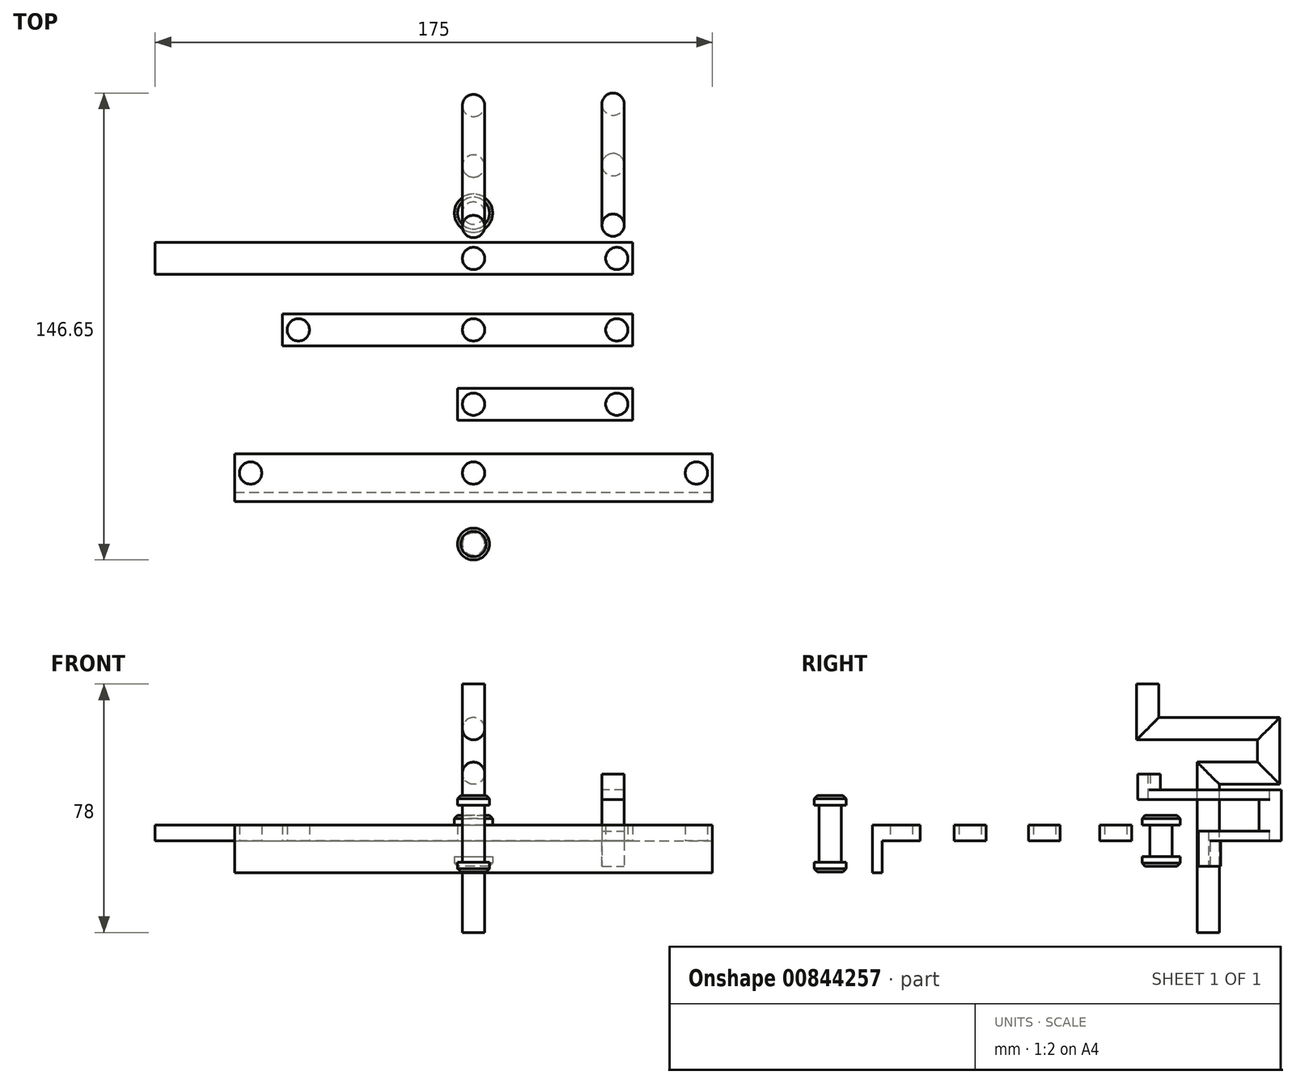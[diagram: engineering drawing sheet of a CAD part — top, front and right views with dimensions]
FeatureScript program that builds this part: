
annotation { "Feature Type Name" : "Feature", "Feature Type Description" : "" }
export const myFeature = defineFeature(function(context is Context, id is Id, definition is map)
    precondition{}
    {
        {
            var Q0;
            Q0=qCreatedBy(makeId("Top.planeOp"),FACE);
            var sketch = newSketch(context, id + "F0", { "sketchPlane" : qUnion([Q0])});
            skLineSegment(sketch, "E0.bottom", {"start": v(50, -5) * mm, "end": v(-60, -5) * mm});
            skLineSegment(sketch, "E0.top", {"start": v(50, 5) * mm, "end": v(-60, 5) * mm});
            skLineSegment(sketch, "E0.left", {"start": v(50, -5) * mm, "end": v(50, 5) * mm});
            skLineSegment(sketch, "E0.right", {"start": v(-60, -5) * mm, "end": v(-60, 5) * mm});
            skPoint(sketch, "E0.middle", {"position": v(0, 0) * mm});
            skCircle(sketch, "E1", {"center": v(-55, 0) * mm, "radius": 3.5 * mm});
            skCircle(sketch, "E2", {"center": v(45, 0) * mm, "radius": 3.5 * mm});
            skPoint(sketch, "E2.centerSnap0", {"position": v(50, 0) * mm});
            skCircle(sketch, "E3", {"center": v(0, 0) * mm, "radius": 3.5 * mm});
            skSolve(sketch);
        }
        {
            var Q0;
            Q0=makeQuery(id+"F0.imprint","IMPRINT",FACE,{"disambiguationData":[TD([[makeQuery(id+"F0.imprint","IMPRINT",EDGE,{"derivedFrom":sQuery(id+"F0.wireOp",EDGE,"E0.bottom")}),-1.0]])]});
            extrude(context, id + "F1", {"entities" : qUnion([Q0]), "depth" : 5 * mm, "offsetDistance" : 25 * mm});
        }
        {
            var Q0;
            Q0=qCreatedBy(makeId("Top.planeOp"),FACE);
            var sketch = newSketch(context, id + "F2", { "sketchPlane" : qUnion([Q0])});
            skLineSegment(sketch, "E4.bottom", {"start": v(-100, 27.42) * mm, "end": v(50, 27.42) * mm});
            skLineSegment(sketch, "E4.top", {"start": v(-100, 17.42) * mm, "end": v(50, 17.42) * mm});
            skLineSegment(sketch, "E4.left", {"start": v(-100, 27.42) * mm, "end": v(-100, 17.42) * mm});
            skLineSegment(sketch, "E4.right", {"start": v(50, 27.42) * mm, "end": v(50, 17.42) * mm});
            skLineSegment(sketch, "E5", {"start": v(-100, 22.42) * mm, "end": v(50, 22.42) * mm, "construction": true});
            skCircle(sketch, "E6", {"center": v(0, 22.42) * mm, "radius": 3.5 * mm});
            skCircle(sketch, "E7", {"center": v(45, 22.42) * mm, "radius": 3.5 * mm});
            skSolve(sketch);
        }
        {
            var Q0;
            Q0=makeQuery(id+"F2.imprint","IMPRINT",FACE,{"disambiguationData":[TD([[makeQuery(id+"F2.imprint","IMPRINT",EDGE,{"derivedFrom":sQuery(id+"F2.wireOp",EDGE,"E4.bottom")}),-1.0]])]});
            extrude(context, id + "F3", {"entities" : qUnion([Q0]), "depth" : 5 * mm, "offsetDistance" : 25 * mm});
        }
        {
            var Q0;
            Q0=qCreatedBy(makeId("Top.planeOp"),FACE);
            var sketch = newSketch(context, id + "F4", { "sketchPlane" : qUnion([Q0])});
            skLineSegment(sketch, "E8.bottom", {"start": v(-5, -18.35) * mm, "end": v(50, -18.35) * mm});
            skLineSegment(sketch, "E8.top", {"start": v(-5, -28.35) * mm, "end": v(50, -28.35) * mm});
            skLineSegment(sketch, "E8.left", {"start": v(-5, -18.35) * mm, "end": v(-5, -28.35) * mm});
            skLineSegment(sketch, "E8.right", {"start": v(50, -18.35) * mm, "end": v(50, -28.35) * mm});
            skLineSegment(sketch, "E9", {"start": v(-5, -23.35) * mm, "end": v(50, -23.35) * mm, "construction": true});
            skCircle(sketch, "E10", {"center": v(0, -23.35) * mm, "radius": 3.5 * mm});
            skCircle(sketch, "E11", {"center": v(45, -23.35) * mm, "radius": 3.5 * mm});
            skSolve(sketch);
        }
        {
            var Q0;
            Q0=makeQuery(id+"F4.imprint","IMPRINT",FACE,{"disambiguationData":[TD([[makeQuery(id+"F4.imprint","IMPRINT",EDGE,{"derivedFrom":sQuery(id+"F4.wireOp",EDGE,"E8.bottom")}),-1.0]])]});
            extrude(context, id + "F5", {"entities" : qUnion([Q0]), "depth" : 5 * mm, "offsetDistance" : 25 * mm});
        }
        {
            var Q0;
            Q0=qCreatedBy(makeId("Top.planeOp"),FACE);
            var sketch = newSketch(context, id + "F6", { "sketchPlane" : qUnion([Q0])});
            skLineSegment(sketch, "E12.bottom", {"start": v(-75, -38.96) * mm, "end": v(75, -38.96) * mm});
            skLineSegment(sketch, "E12.top", {"start": v(-75, -53.96) * mm, "end": v(75, -53.96) * mm});
            skLineSegment(sketch, "E12.left", {"start": v(-75, -38.96) * mm, "end": v(-75, -53.96) * mm});
            skLineSegment(sketch, "E12.right", {"start": v(75, -38.96) * mm, "end": v(75, -53.96) * mm});
            skLineSegment(sketch, "E13", {"start": v(-75, -50.96) * mm, "end": v(75, -50.96) * mm});
            skLineSegment(sketch, "E14", {"start": v(-75, -44.96) * mm, "end": v(75, -44.96) * mm, "construction": true});
            skCircle(sketch, "E15", {"center": v(-70, -44.96) * mm, "radius": 3.5 * mm});
            skCircle(sketch, "E16", {"center": v(0, -44.96) * mm, "radius": 3.5 * mm});
            skCircle(sketch, "E17", {"center": v(70, -44.96) * mm, "radius": 3.5 * mm});
            skSolve(sketch);
        }
        {
            var Q0;
            {var subQ1=sQuery(id+"F6.wireOp",EDGE,"E12.top");Q0=makeQuery(id+"F6.imprint","IMPRINT",FACE,{"disambiguationData":[TD([[makeQuery(id+"F6.imprint","IMPRINT",EDGE,{"derivedFrom":subQ1}),1.0]])]});}
            var Q1;
            {var subQ0=sQuery(id+"F6.wireOp",EDGE,"E16");var subQ1=sQuery(id+"F6.wireOp",EDGE,"E13");var subQ2=makeQuery(id+"F6.imprint","INTERSECT",VERTEX,{"disambiguationData":[OD(0.0)],"derivedFrom":[subQ1,subQ0]});Q1=makeQuery(id+"F6.imprint","IMPRINT",FACE,{"disambiguationData":[TD([[makeQuery(id+"F6.imprint","IMPRINT",EDGE,{"disambiguationData":[TD([[subQ2,-1.0]])],"derivedFrom":subQ1}),-1.0]])]});}
            var Q2;
            {var subQ0=sQuery(id+"F6.wireOp",EDGE,"E15");var subQ1=sQuery(id+"F6.wireOp",EDGE,"E13");var subQ2=makeQuery(id+"F6.imprint","INTERSECT",VERTEX,{"disambiguationData":[OD(0.0)],"derivedFrom":[subQ1,subQ0]});Q2=makeQuery(id+"F6.imprint","IMPRINT",FACE,{"disambiguationData":[TD([[makeQuery(id+"F6.imprint","IMPRINT",EDGE,{"disambiguationData":[TD([[subQ2,-1.0]])],"derivedFrom":subQ1}),-1.0]])]});}
            var Q3;
            {var subQ0=sQuery(id+"F6.wireOp",EDGE,"E17");var subQ1=sQuery(id+"F6.wireOp",EDGE,"E13");var subQ2=makeQuery(id+"F6.imprint","INTERSECT",VERTEX,{"disambiguationData":[OD(0.0)],"derivedFrom":[subQ1,subQ0]});Q3=makeQuery(id+"F6.imprint","IMPRINT",FACE,{"disambiguationData":[TD([[makeQuery(id+"F6.imprint","IMPRINT",EDGE,{"disambiguationData":[TD([[subQ2,-1.0]])],"derivedFrom":subQ1}),-1.0]])]});}
            extrude(context, id + "F7", {"entities" : qUnion([Q0, Q1, Q2, Q3]), "oppositeDirection" : true, "depth" : 10 * mm, "offsetDistance" : 25 * mm});
        }
        {
            var Q0;
            {var subQ6=sQuery(id+"F6.wireOp",EDGE,"E12.bottom");Q0=makeQuery(id+"F6.imprint","IMPRINT",FACE,{"disambiguationData":[TD([[makeQuery(id+"F6.imprint","IMPRINT",EDGE,{"derivedFrom":subQ6}),-1.0]])]});}
            var Q1;
            {var subQ1=sQuery(id+"F6.wireOp",EDGE,"E12.top");Q1=makeQuery(id+"F6.imprint","IMPRINT",FACE,{"disambiguationData":[TD([[makeQuery(id+"F6.imprint","IMPRINT",EDGE,{"derivedFrom":subQ1}),1.0]])]});}
            extrude(context, id + "F8", {"entities" : qUnion([Q0, Q1]), "operationType" : NewBodyOperationType.ADD, "depth" : 5 * mm, "offsetDistance" : 25 * mm});
        }
        {
            var Q0;
            Q0=qCreatedBy(makeId("Right.planeOp"),FACE);
            var sketch = newSketch(context, id + "F9", { "sketchPlane" : qUnion([Q0])});
            skLineSegment(sketch, "E18", {"start": v(36.67, -15.56) * mm, "end": v(36.67, 16.44) * mm, "construction": true});
            skLineSegment(sketch, "E19.MirrorCS", {"start": v(30.67, -5) * mm, "end": v(30.67, -8) * mm});
            skLineSegment(sketch, "E20.MirrorCS", {"start": v(33.17, -5) * mm, "end": v(30.67, -5) * mm});
            skLineSegment(sketch, "E21.MirrorCS", {"start": v(30.67, -8) * mm, "end": v(36.67, -8) * mm});
            skLineSegment(sketch, "E22.MirrorCS", {"start": v(33.17, 0) * mm, "end": v(33.17, -5) * mm});
            skLineSegment(sketch, "E23.MirrorCS", {"start": v(30.67, 8) * mm, "end": v(36.67, 8) * mm});
            skLineSegment(sketch, "E24.MirrorCS", {"start": v(30.67, 5) * mm, "end": v(30.67, 8) * mm});
            skLineSegment(sketch, "E25.MirrorCS", {"start": v(33.17, 0) * mm, "end": v(33.17, 5) * mm});
            skLineSegment(sketch, "E26.MirrorCS", {"start": v(33.17, 5) * mm, "end": v(30.67, 5) * mm});
            skLineSegment(sketch, "E27", {"start": v(36.67, 8) * mm, "end": v(36.67, -8) * mm});
            skSolve(sketch);
        }
        {
            var Q0;
            Q0=makeQuery(id+"F9.imprint","IMPRINT",FACE,{"disambiguationData":[TD([[makeQuery(id+"F9.imprint","IMPRINT",EDGE,{"derivedFrom":sQuery(id+"F9.wireOp",EDGE,"E19.MirrorCS")}),1.0]])]});
            var Q1;
            Q1=sQuery(id+"F9.wireOp",EDGE,"E18");
            revolve(context, id + "F10", {"surfaceOperationType" : NewSurfaceOperationType.NEW, "entities" : qUnion([Q0]), "axis" : qUnion([Q1]), "revolveType" : RevolveType.FULL});
        }
        {
            var Q0;
            Q0=makeQuery(id+"F10.opRevolve","SWEPT_EDGE",EDGE,{"disambiguationData":[OSD([sQuery(id+"F9.wireOp",EDGE,"E23.MirrorCS"),sQuery(id+"F9.wireOp",EDGE,"E24.MirrorCS")])]});
            var Q1;
            Q1=makeQuery(id+"F10.opRevolve","SWEPT_EDGE",EDGE,{"disambiguationData":[OSD([sQuery(id+"F9.wireOp",EDGE,"E19.MirrorCS"),sQuery(id+"F9.wireOp",EDGE,"E21.MirrorCS")])]});
            chamfer(context, id + "F11", {"entities" : qUnion([Q0, Q1]), "width" : 1 * mm, "tangentPropagation" : true});
        }
        {
            var Q0;
            Q0=qCreatedBy(makeId("Right.planeOp"),FACE);
            var sketch = newSketch(context, id + "F12", { "sketchPlane" : qUnion([Q0])});
            skLineSegment(sketch, "E28", {"start": v(51.47, 21.22) * mm, "end": v(51.47, -28.78) * mm});
            skLineSegment(sketch, "E29", {"start": v(51.47, 21.22) * mm, "end": v(70.47, 21.22) * mm});
            skLineSegment(sketch, "E30", {"start": v(70.47, 21.22) * mm, "end": v(70.47, 35.22) * mm});
            skLineSegment(sketch, "E31", {"start": v(70.47, 35.22) * mm, "end": v(32.47, 35.22) * mm});
            skLineSegment(sketch, "E32", {"start": v(32.47, 35.22) * mm, "end": v(32.47, 49.22) * mm});
            skSolve(sketch);
        }
        {
            var Q0;
            Q0=qCreatedBy(makeId("Top.planeOp"),FACE);
            var Q1;
            Q1=sQuery(id+"F12.wireOp",VERTEX,"E28.end");
            cPlane(context, id + "F13", {"entities" : qUnion([Q0, Q1]), "cplaneType" : CPlaneType.PLANE_POINT, "offset" : 25 * mm, "width" : 150 * mm, "height" : 150 * mm});
        }
        {
            var Q0;
            Q0=qCreatedBy(id+"F13.planeOp",FACE);
            var sketch = newSketch(context, id + "F14", { "sketchPlane" : qUnion([Q0])});
            skCircle(sketch, "E33", {"center": v(0, 51.47) * mm, "radius": 3.5 * mm});
            skSolve(sketch);
        }
        {
            var Q0;
            Q0=makeQuery(id+"F14.imprint","IMPRINT",FACE,{"disambiguationData":[TD([[makeQuery(id+"F14.imprint","IMPRINT",EDGE,{"derivedFrom":sQuery(id+"F14.wireOp",EDGE,"E33")}),1.0]])]});
            var Q1;
            Q1=sQuery(id+"F12.wireOp",EDGE,"E28");
            var Q2;
            Q2=sQuery(id+"F12.wireOp",EDGE,"E29");
            var Q3;
            Q3=sQuery(id+"F12.wireOp",EDGE,"E30");
            var Q4;
            Q4=sQuery(id+"F12.wireOp",EDGE,"E31");
            var Q5;
            Q5=sQuery(id+"F12.wireOp",EDGE,"E32");
            sweep(context, id + "F15", {"profiles" : qUnion([Q0]), "path" : qUnion([Q1, Q2, Q3, Q4, Q5])});
        }
        {
            var Q0;
            Q0=qCreatedBy(makeId("Right.planeOp"),FACE);
            var sketch = newSketch(context, id + "F16", { "sketchPlane" : qUnion([Q0])});
            skLineSegment(sketch, "E34", {"start": v(-67.26, 14.23) * mm, "end": v(-67.26, -9.77) * mm});
            skLineSegment(sketch, "E35", {"start": v(-72.26, -9.77) * mm, "end": v(-72.26, -6.77) * mm});
            skLineSegment(sketch, "E36", {"start": v(-72.26, -6.77) * mm, "end": v(-70.76, -6.77) * mm});
            skLineSegment(sketch, "E37", {"start": v(-70.76, -6.77) * mm, "end": v(-70.76, 3.23) * mm});
            skLineSegment(sketch, "E38", {"start": v(-70.76, 3.23) * mm, "end": v(-70.76, 3.23) * mm});
            skLineSegment(sketch, "E39", {"start": v(-70.76, 3.23) * mm, "end": v(-70.76, 6.23) * mm});
            skLineSegment(sketch, "E40", {"start": v(-70.76, 6.23) * mm, "end": v(-70.76, 6.23) * mm});
            skLineSegment(sketch, "E41", {"start": v(-70.76, 6.23) * mm, "end": v(-70.76, 11.23) * mm});
            skLineSegment(sketch, "E42", {"start": v(-70.76, 11.23) * mm, "end": v(-72.26, 11.23) * mm});
            skLineSegment(sketch, "E43", {"start": v(-72.26, 11.23) * mm, "end": v(-72.26, 14.23) * mm});
            skLineSegment(sketch, "E44", {"start": v(-72.26, 14.23) * mm, "end": v(-67.26, 14.23) * mm});
            skLineSegment(sketch, "E45", {"start": v(-72.26, -9.77) * mm, "end": v(-67.26, -9.77) * mm});
            skSolve(sketch);
        }
        {
            var Q0;
            Q0=makeQuery(id+"F16.imprint","IMPRINT",FACE,{"disambiguationData":[TD([[makeQuery(id+"F16.imprint","IMPRINT",EDGE,{"derivedFrom":sQuery(id+"F16.wireOp",EDGE,"E34")}),-1.0]])]});
            var Q1;
            Q1=sQuery(id+"F16.wireOp",EDGE,"E34");
            revolve(context, id + "F17", {"surfaceOperationType" : NewSurfaceOperationType.NEW, "entities" : qUnion([Q0]), "axis" : qUnion([Q1]), "revolveType" : RevolveType.FULL});
        }
        {
            var Q0;
            Q0=makeQuery(id+"F17.opRevolve","SWEPT_EDGE",EDGE,{"disambiguationData":[OSD([sQuery(id+"F16.wireOp",EDGE,"E35"),sQuery(id+"F16.wireOp",EDGE,"E45")])]});
            var Q1;
            Q1=makeQuery(id+"F17.opRevolve","SWEPT_EDGE",EDGE,{"disambiguationData":[OSD([sQuery(id+"F16.wireOp",EDGE,"E43"),sQuery(id+"F16.wireOp",EDGE,"E44")])]});
            chamfer(context, id + "F18", {"entities" : qUnion([Q0, Q1]), "width" : 1 * mm, "tangentPropagation" : true});
        }
        {
            var Q0;
            Q0=qCreatedBy(makeId("Top.planeOp"),FACE);
            var sketch = newSketch(context, id + "F19", { "sketchPlane" : qUnion([Q0])});
            skCircle(sketch, "E46", {"center": v(43.82, 32.89) * mm, "radius": 3.5 * mm});
            skLineSegment(sketch, "E47", {"start": v(43.82, 32.89) * mm, "end": v(43.82, 70.89) * mm, "construction": true});
            skCircle(sketch, "E48", {"center": v(43.82, 70.89) * mm, "radius": 3.5 * mm});
            skCircle(sketch, "E49", {"center": v(43.82, 51.89) * mm, "radius": 3.5 * mm});
            skLineSegment(sketch, "E50", {"start": v(40.33, 70.56) * mm, "end": v(40.33, 51.56) * mm});
            skLineSegment(sketch, "E51", {"start": v(40.33, 51.56) * mm, "end": v(40.33, 32.56) * mm});
            skLineSegment(sketch, "E52", {"start": v(47.32, 32.89) * mm, "end": v(47.32, 51.89) * mm});
            skLineSegment(sketch, "E53", {"start": v(47.32, 51.89) * mm, "end": v(47.32, 70.89) * mm});
            skSolve(sketch);
        }
        {
            var Q0;
            {var subQ1=sQuery(id+"F19.wireOp",EDGE,"E49");var subQ3=sQuery(id+"F19.wireOp",EDGE,"E50");var subQ4=makeQuery(id+"F19.imprint","INTERSECT",VERTEX,{"derivedFrom":[subQ1,subQ3]});Q0=makeQuery(id+"F19.imprint","IMPRINT",FACE,{"disambiguationData":[TD([[makeQuery(id+"F19.imprint","IMPRINT",EDGE,{"disambiguationData":[TD([[subQ4,1.0]])],"derivedFrom":subQ1}),1.0]])]});}
            var Q1;
            {var subQ3=sQuery(id+"F19.wireOp",EDGE,"E53");Q1=makeQuery(id+"F19.imprint","IMPRINT",FACE,{"disambiguationData":[TD([[makeQuery(id+"F19.imprint","IMPRINT",EDGE,{"derivedFrom":subQ3}),1.0]])]});}
            var Q2;
            {var subQ0=sQuery(id+"F19.wireOp",EDGE,"E48");var subQ1=makeQuery(id+"F19.imprint","INTERSECT",VERTEX,{"derivedFrom":[subQ0,sQuery(id+"F19.wireOp",EDGE,"E50")]});Q2=makeQuery(id+"F19.imprint","IMPRINT",FACE,{"disambiguationData":[TD([[makeQuery(id+"F19.imprint","IMPRINT",EDGE,{"disambiguationData":[TD([[subQ1,-1.0]])],"derivedFrom":subQ0}),1.0]])]});}
            extrude(context, id + "F20", {"entities" : qUnion([Q0, Q1, Q2]), "depth" : 3 * mm, "offsetDistance" : 25 * mm});
        }
        {
            var Q0;
            {var subQ1=sQuery(id+"F19.wireOp",EDGE,"E49");var subQ3=sQuery(id+"F19.wireOp",EDGE,"E50");var subQ4=makeQuery(id+"F19.imprint","INTERSECT",VERTEX,{"derivedFrom":[subQ1,subQ3]});Q0=makeQuery(id+"F19.imprint","IMPRINT",FACE,{"disambiguationData":[TD([[makeQuery(id+"F19.imprint","IMPRINT",EDGE,{"disambiguationData":[TD([[subQ4,1.0]])],"derivedFrom":subQ1}),1.0]])]});}
            var Q1;
            Q1=sQuery(id+"F19.wireOp",EDGE,"E49");
            extrude(context, id + "F21", {"entities" : qUnion([Q0]), "surfaceEntities" : qUnion([Q1]), "oppositeDirection" : true, "depth" : 5 * mm, "offsetDistance" : 25 * mm});
        }
        {
            var Q0;
            {var subQ0=sQuery(id+"F19.wireOp",EDGE,"E48");var subQ1=makeQuery(id+"F19.imprint","INTERSECT",VERTEX,{"derivedFrom":[subQ0,sQuery(id+"F19.wireOp",EDGE,"E50")]});Q0=makeQuery(id+"F19.imprint","IMPRINT",FACE,{"disambiguationData":[TD([[makeQuery(id+"F19.imprint","IMPRINT",EDGE,{"disambiguationData":[TD([[subQ1,-1.0]])],"derivedFrom":subQ0}),1.0]])]});}
            var Q1;
            Q1=sQuery(id+"F19.wireOp",EDGE,"E48");
            extrude(context, id + "F22", {"entities" : qUnion([Q0]), "surfaceEntities" : qUnion([Q1]), "depth" : 13 * mm, "offsetDistance" : 25 * mm});
        }
        {
            var Q0;
            Q0=makeQuery(id+"F21.opExtrude","SWEPT_BODY",BODY,{"disambiguationData":[OSD([sQuery(id+"F19.wireOp",EDGE,"E49"),sQuery(id+"F19.wireOp",EDGE,"E50"),sQuery(id+"F19.wireOp",EDGE,"E52")])]});
            var Q1;
            Q1=makeQuery(id+"F22.opExtrude","SWEPT_BODY",BODY,{"disambiguationData":[OSD([sQuery(id+"F19.wireOp",EDGE,"E48")])]});
            deleteBodies(context, id + "F23", {"entities" : qUnion([Q0, Q1])});
        }
        {
            var Q0;
            {var subQ0=sQuery(id+"F19.wireOp",EDGE,"E48");var subQ1=makeQuery(id+"F19.imprint","INTERSECT",VERTEX,{"derivedFrom":[subQ0,sQuery(id+"F19.wireOp",EDGE,"E50")]});Q0=makeQuery(id+"F19.imprint","IMPRINT",FACE,{"disambiguationData":[TD([[makeQuery(id+"F19.imprint","IMPRINT",EDGE,{"disambiguationData":[TD([[subQ1,-1.0]])],"derivedFrom":subQ0}),1.0]])]});}
            extrude(context, id + "F24", {"entities" : qUnion([Q0]), "operationType" : NewBodyOperationType.ADD, "depth" : 13 * mm, "offsetDistance" : 25 * mm});
        }
        {
            var Q0;
            Q0=makeQuery(id+"F24.opExtrude","CAP_FACE",FACE,{"disambiguationData":[OSD([sQuery(id+"F19.wireOp",EDGE,"E48")])],"isStart":false});
            cPlane(context, id + "F25", {"entities" : qUnion([Q0]), "cplaneType" : CPlaneType.OFFSET, "offset" : 0 * mm, "width" : 150 * mm, "height" : 150 * mm});
        }
        {
            var Q0;
            Q0=qCreatedBy(id+"F25.planeOp",FACE);
            var sketch = newSketch(context, id + "F26", { "sketchPlane" : qUnion([Q0])});
            skCircle(sketch, "E54", {"center": v(43.82, 32.89) * mm, "radius": 3.5 * mm});
            skLineSegment(sketch, "E55", {"start": v(43.82, 32.89) * mm, "end": v(43.82, 70.89) * mm, "construction": true});
            skCircle(sketch, "E56", {"center": v(43.82, 70.89) * mm, "radius": 3.5 * mm});
            skCircle(sketch, "E57", {"center": v(43.82, 51.89) * mm, "radius": 3.5 * mm});
            skLineSegment(sketch, "E58", {"start": v(40.33, 70.56) * mm, "end": v(40.33, 51.56) * mm});
            skLineSegment(sketch, "E59", {"start": v(40.33, 51.56) * mm, "end": v(40.33, 32.56) * mm});
            skLineSegment(sketch, "E60", {"start": v(47.32, 32.89) * mm, "end": v(47.32, 51.89) * mm});
            skLineSegment(sketch, "E61", {"start": v(47.32, 51.89) * mm, "end": v(47.32, 70.89) * mm});
            skSolve(sketch);
        }
        {
            var Q0;
            {var subQ0=sQuery(id+"F26.wireOp",EDGE,"E56");var subQ1=makeQuery(id+"F26.imprint","INTERSECT",VERTEX,{"derivedFrom":[subQ0,sQuery(id+"F26.wireOp",EDGE,"E58")]});Q0=makeQuery(id+"F26.imprint","IMPRINT",FACE,{"disambiguationData":[TD([[makeQuery(id+"F26.imprint","IMPRINT",EDGE,{"disambiguationData":[TD([[subQ1,1.0]])],"derivedFrom":subQ0}),1.0]])]});}
            var Q1;
            {var subQ3=sQuery(id+"F26.wireOp",EDGE,"E61");Q1=makeQuery(id+"F26.imprint","IMPRINT",FACE,{"disambiguationData":[TD([[makeQuery(id+"F26.imprint","IMPRINT",EDGE,{"derivedFrom":subQ3}),1.0]])]});}
            var Q2;
            {var subQ0=sQuery(id+"F26.wireOp",EDGE,"E57");var subQ1=makeQuery(id+"F26.imprint","INTERSECT",VERTEX,{"derivedFrom":[subQ0,sQuery(id+"F26.wireOp",EDGE,"E61")]});Q2=makeQuery(id+"F26.imprint","IMPRINT",FACE,{"disambiguationData":[TD([[makeQuery(id+"F26.imprint","IMPRINT",EDGE,{"disambiguationData":[TD([[subQ1,-1.0]])],"derivedFrom":subQ0}),1.0]])]});}
            var Q3;
            {var subQ0=sQuery(id+"F26.wireOp",EDGE,"E60");Q3=makeQuery(id+"F26.imprint","IMPRINT",FACE,{"disambiguationData":[TD([[makeQuery(id+"F26.imprint","IMPRINT",EDGE,{"derivedFrom":subQ0}),1.0]])]});}
            var Q4;
            {var subQ0=sQuery(id+"F26.wireOp",EDGE,"E54");var subQ1=makeQuery(id+"F26.imprint","INTERSECT",VERTEX,{"derivedFrom":[subQ0,sQuery(id+"F26.wireOp",EDGE,"E60")]});Q4=makeQuery(id+"F26.imprint","IMPRINT",FACE,{"disambiguationData":[TD([[makeQuery(id+"F26.imprint","IMPRINT",EDGE,{"disambiguationData":[TD([[subQ1,-1.0]])],"derivedFrom":subQ0}),1.0]])]});}
            extrude(context, id + "F27", {"entities" : qUnion([Q0, Q1, Q2, Q3, Q4]), "operationType" : NewBodyOperationType.ADD, "depth" : 3 * mm, "offsetDistance" : 25 * mm});
        }
        {
            var Q0;
            {var subQ0=sQuery(id+"F26.wireOp",EDGE,"E54");var subQ1=makeQuery(id+"F26.imprint","INTERSECT",VERTEX,{"derivedFrom":[subQ0,sQuery(id+"F26.wireOp",EDGE,"E60")]});Q0=makeQuery(id+"F26.imprint","IMPRINT",FACE,{"disambiguationData":[TD([[makeQuery(id+"F26.imprint","IMPRINT",EDGE,{"disambiguationData":[TD([[subQ1,-1.0]])],"derivedFrom":subQ0}),1.0]])]});}
            extrude(context, id + "F28", {"entities" : qUnion([Q0]), "operationType" : NewBodyOperationType.ADD, "depth" : 8 * mm, "offsetDistance" : 25 * mm});
        }
        {
            var Q0;
            {var subQ0=sQuery(id+"F19.wireOp",EDGE,"E49");var subQ1=makeQuery(id+"F19.imprint","INTERSECT",VERTEX,{"derivedFrom":[subQ0,sQuery(id+"F19.wireOp",EDGE,"E53")]});Q0=makeQuery(id+"F19.imprint","IMPRINT",FACE,{"disambiguationData":[TD([[makeQuery(id+"F19.imprint","IMPRINT",EDGE,{"disambiguationData":[TD([[subQ1,-1.0]])],"derivedFrom":subQ0}),1.0]])]});}
            extrude(context, id + "F29", {"entities" : qUnion([Q0]), "operationType" : NewBodyOperationType.ADD, "oppositeDirection" : true, "depth" : 8 * mm, "offsetDistance" : 25 * mm});
        }
    });
